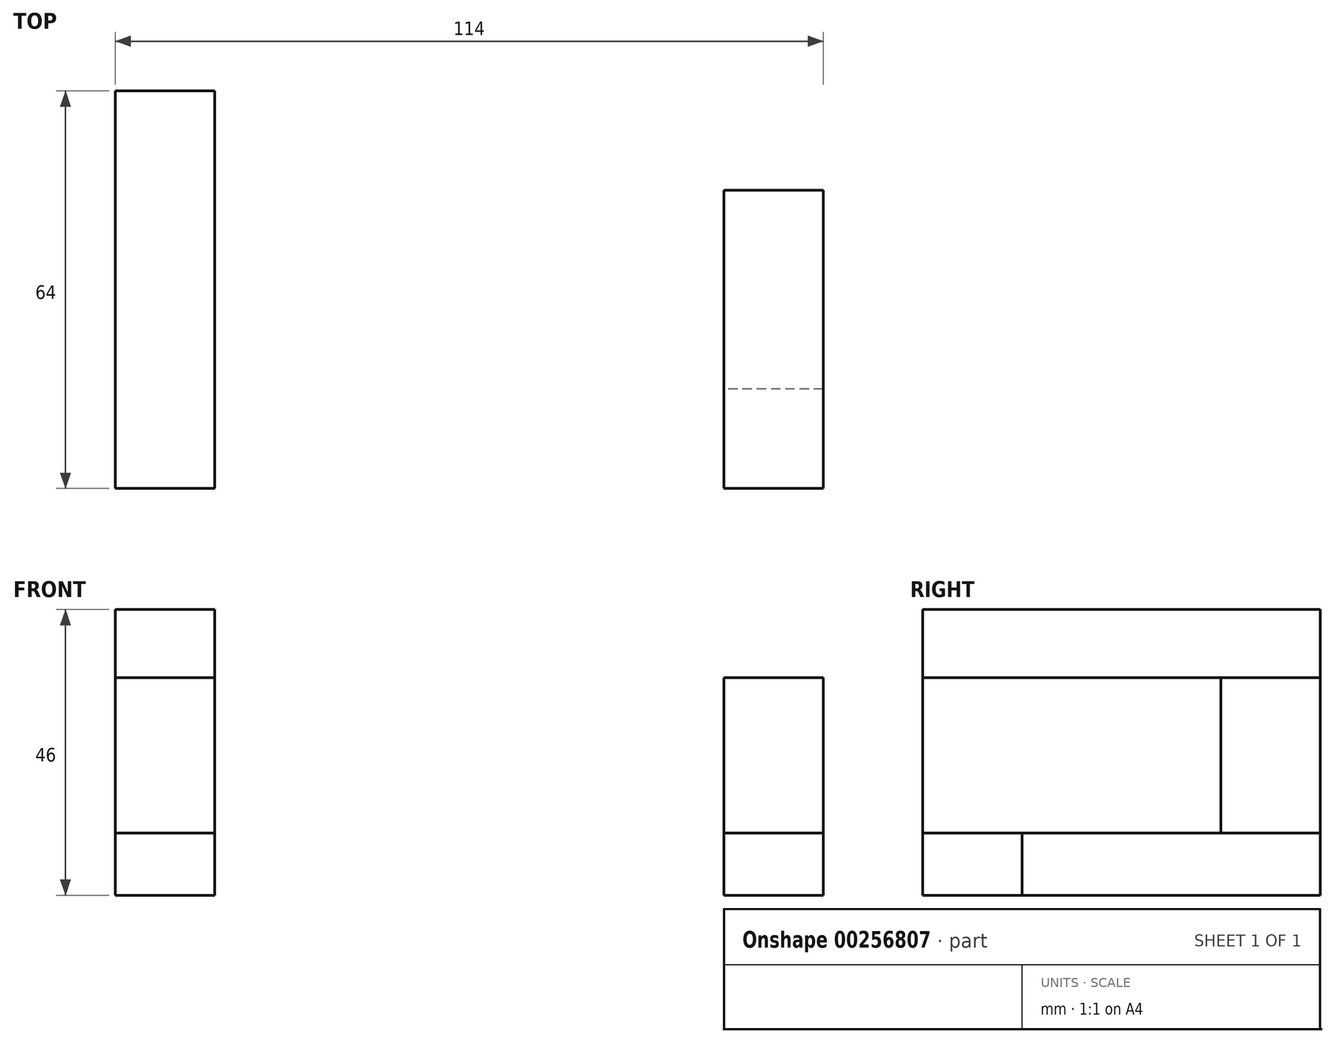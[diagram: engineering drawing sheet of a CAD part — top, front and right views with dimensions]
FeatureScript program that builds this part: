
annotation { "Feature Type Name" : "Feature", "Feature Type Description" : "" }
export const myFeature = defineFeature(function(context is Context, id is Id, definition is map)
    precondition{}
    {
        {
            var Q0;
            Q0=qCreatedBy(makeId("Top.planeOp"),FACE);
            var sketch = newSketch(context, id + "F0", { "sketchPlane" : qUnion([Q0])});
            skLineSegment(sketch, "E0", {"start": v(-57, -23.66) * mm, "end": v(57, -23.66) * mm});
            skLineSegment(sketch, "E1", {"start": v(57, -23.66) * mm, "end": v(57, 40.34) * mm});
            skLineSegment(sketch, "E2", {"start": v(57, 40.34) * mm, "end": v(-57, 40.34) * mm});
            skLineSegment(sketch, "E3", {"start": v(-57, 40.34) * mm, "end": v(-57, -23.66) * mm});
            skLineSegment(sketch, "E4", {"start": v(57, -23.66) * mm, "end": v(57, -7.66) * mm});
            skLineSegment(sketch, "E5", {"start": v(57, -23.66) * mm, "end": v(41, -23.66) * mm});
            skLineSegment(sketch, "E6", {"start": v(41, -23.66) * mm, "end": v(41, 40.34) * mm});
            skLineSegment(sketch, "E7", {"start": v(41, 40.34) * mm, "end": v(41, 24.34) * mm});
            skLineSegment(sketch, "E8", {"start": v(41, 24.34) * mm, "end": v(57, 24.34) * mm});
            skLineSegment(sketch, "E9", {"start": v(57, -7.66) * mm, "end": v(41, -7.66) * mm});
            skLineSegment(sketch, "E10", {"start": v(-57, -23.66) * mm, "end": v(-41, -23.66) * mm});
            skLineSegment(sketch, "E11", {"start": v(-41, -23.66) * mm, "end": v(-41, 40.34) * mm});
            skLineSegment(sketch, "E12", {"start": v(57, -23.66) * mm, "end": v(0, -23.66) * mm});
            skLineSegment(sketch, "E13", {"start": v(0, -23.66) * mm, "end": v(0, 40.34) * mm});
            skPoint(sketch, "E14.endSnap0", {"position": v(0, 8.34) * mm});
            skCircle(sketch, "E15", {"center": v(-21, 8.34) * mm, "radius": 10 * mm});
            skCircle(sketch, "E16", {"center": v(20, 8.34) * mm, "radius": 10 * mm});
            skSolve(sketch);
        }
        {
            var Q0;
            Q0=makeQuery(id+"F0.imprint","IMPRINT",FACE,{"disambiguationData":[TD([[makeQuery(id+"F0.imprint","IMPRINT",EDGE,{"derivedFrom":sQuery(id+"F0.wireOp",EDGE,"E0")}),1.0]])]});
            var Q1;
            {var subQ0=sQuery(id+"F0.wireOp",EDGE,"E3");Q1=makeQuery(id+"F0.imprint","IMPRINT",FACE,{"disambiguationData":[TD([[makeQuery(id+"F0.imprint","IMPRINT",EDGE,{"derivedFrom":subQ0}),1.0]])]});}
            extrude(context, id + "F1", {"entities" : qUnion([Q0, Q1]), "oppositeDirection" : true, "depth" : 10 * mm});
        }
        {
            var Q0;
            {var subQ4=sQuery(id+"F0.wireOp",EDGE,"E7");Q0=makeQuery(id+"F0.imprint","IMPRINT",FACE,{"disambiguationData":[TD([[makeQuery(id+"F0.imprint","IMPRINT",EDGE,{"derivedFrom":subQ4}),1.0]])]});}
            var Q1;
            {var subQ0=sQuery(id+"F0.wireOp",EDGE,"E4");Q1=makeQuery(id+"F0.imprint","IMPRINT",FACE,{"disambiguationData":[TD([[makeQuery(id+"F0.imprint","IMPRINT",EDGE,{"derivedFrom":subQ0}),1.0]])]});}
            var Q2;
            {var subQ0=sQuery(id+"F0.wireOp",EDGE,"E3");Q2=makeQuery(id+"F0.imprint","IMPRINT",FACE,{"disambiguationData":[TD([[makeQuery(id+"F0.imprint","IMPRINT",EDGE,{"derivedFrom":subQ0}),1.0]])]});}
            extrude(context, id + "F2", {"entities" : qUnion([Q0, Q1, Q2]), "operationType" : NewBodyOperationType.ADD, "depth" : 36 * mm});
        }
        {
            var Q0;
            Q0=makeQuery(id+"F0.imprint","IMPRINT",FACE,{"disambiguationData":[TD([[makeQuery(id+"F0.imprint","IMPRINT",EDGE,{"derivedFrom":sQuery(id+"F0.wireOp",EDGE,"E0")}),1.0]])]});
            var Q1;
            {var subQ0=sQuery(id+"F0.wireOp",EDGE,"E7");Q1=makeQuery(id+"F0.imprint","IMPRINT",FACE,{"disambiguationData":[TD([[makeQuery(id+"F0.imprint","IMPRINT",EDGE,{"derivedFrom":subQ0}),-1.0]])]});}
            var Q2;
            {var subQ2=sQuery(id+"F0.wireOp",EDGE,"E8");Q2=makeQuery(id+"F0.imprint","IMPRINT",FACE,{"disambiguationData":[TD([[makeQuery(id+"F0.imprint","IMPRINT",EDGE,{"derivedFrom":subQ2}),-1.0]])]});}
            extrude(context, id + "F3", {"entities" : qUnion([Q0, Q1, Q2]), "depth" : 25 * mm});
        }
    });
